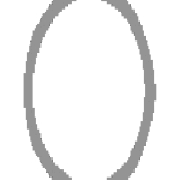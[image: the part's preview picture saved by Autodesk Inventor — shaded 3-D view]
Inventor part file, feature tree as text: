
AUTODESK INVENTOR PART (.ipt)
format: ipt  version: 2021 (Build 250183000, 183)  size: 112,640 bytes
history: native  units: in
note: dims shown in document units (in); Inventor stores cm internally (conversion verified against a paired STEP export)
features: other x4, sketch x3, plane x1
ambient origin geometry x8: Origin, YZ Plane, XZ Plane, XY Plane, X Axis, Y Axis, Z Axis, Center Point
bodies: Solid1 (feature_tree), Body (feature_tree)
feature tree (8):
  other  "Driven Length"
  other  "Frame Generator"
  other  "Start Plane"
  other  "End Plane"
  sketch  "Sketch"  dims[d2=14.4605in d4=-0.0in d5=14.4605in d6=0.12in d7=0.0in d8=90.0deg d9=14.4605in]
  sketch  "Sketch2"  dims[d0=1.0in]
  plane  "Work Plane3"
  sketch  "Sketch3"  dims[d1=0.065in]
